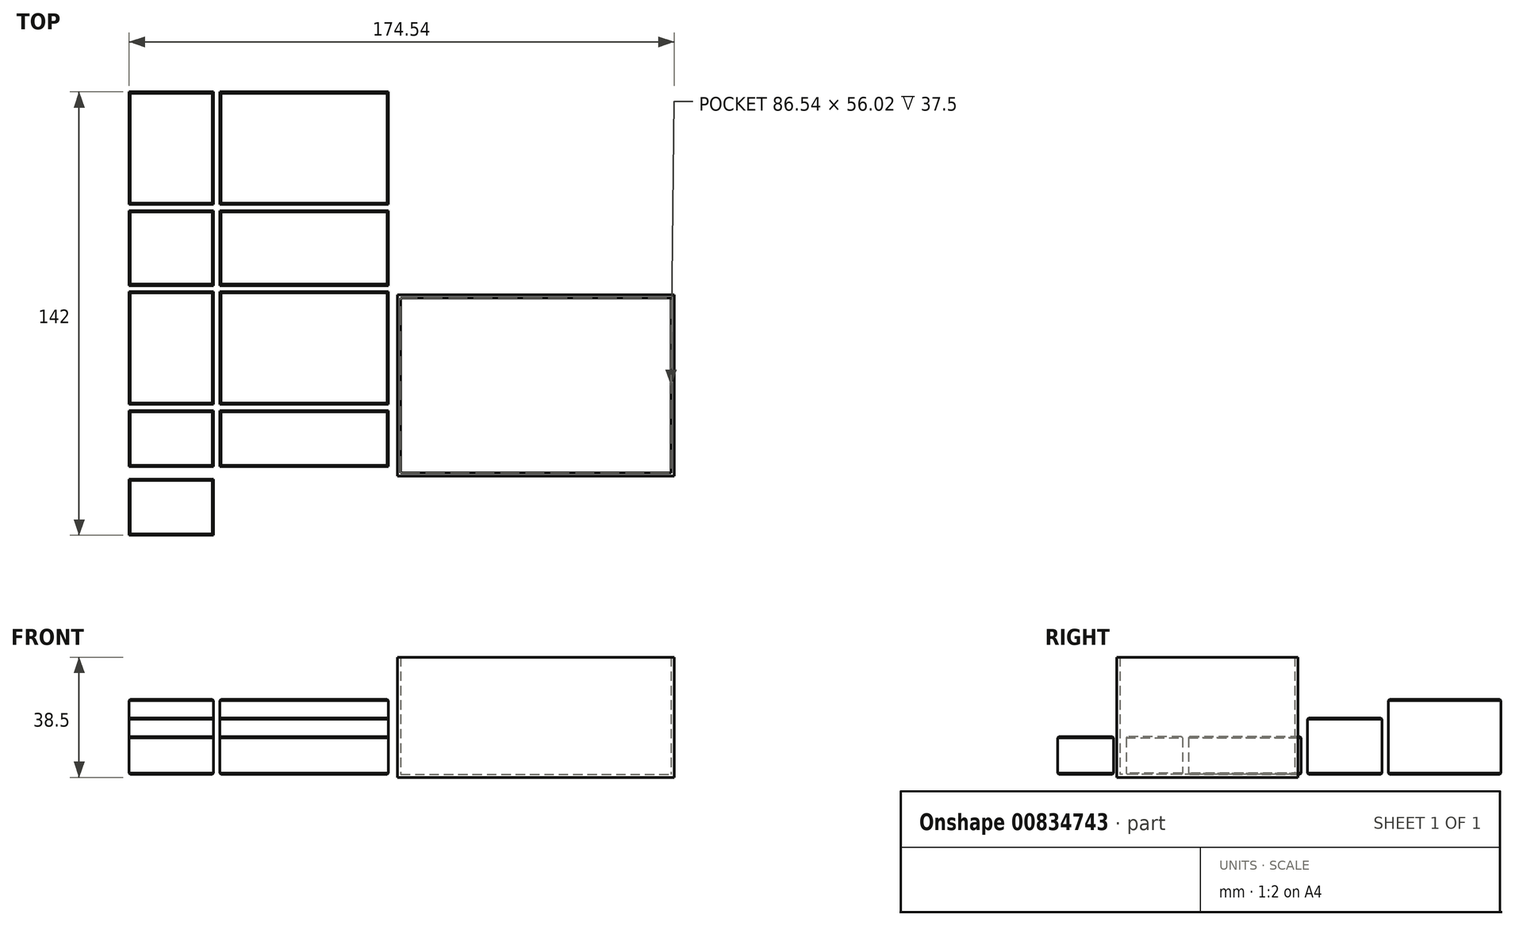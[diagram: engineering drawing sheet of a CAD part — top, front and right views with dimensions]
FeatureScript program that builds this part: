
annotation { "Feature Type Name" : "Feature", "Feature Type Description" : "" }
export const myFeature = defineFeature(function(context is Context, id is Id, definition is map)
    precondition{}
    {
        {
            assignVariable(context, id + "F0", {"name" : "L", "anyValue" : 84});
        }
        {
            assignVariable(context, id + "F1", {"name" : "W", "anyValue" : 9 * getVariable(context, 'L') / 14});
        }
        {
            assignVariable(context, id + "F2", {"name" : "H", "anyValue" : 3 * getVariable(context, 'L') / 7});
        }
        {
            assignVariable(context, id + "F3", {"name" : "A", "anyValue" : getVariable(context, 'L') / 7});
        }
        {
            assignVariable(context, id + "F4", {"name" : "B", "anyValue" : getVariable(context, 'W') / 2});
        }
        {
            assignVariable(context, id + "F5", {"name" : "C", "anyValue" : getVariable(context, 'H') / 2});
        }
        {
            assignVariable(context, id + "F6", {"name" : "NxtSDiff", "anyValue" : (5 * getVariable(context, 'A') + getVariable(context, 'B') - getVariable(context, 'L'))});
        }
        {
            assignVariable(context, id + "F7", {"name" : "H_Box", "anyValue" : getVariable(context, 'NxtSDiff') / 2 + getVariable(context, 'H')});
        }
        {
            assignVariable(context, id + "F8", {"name" : "T_Box", "anyValue" : 1});
        }
        {
            var Q0;
            Q0=qCreatedBy(makeId("Top.planeOp"),FACE);
            var sketch = newSketch(context, id + "F9", { "sketchPlane" : qUnion([Q0])});
            skLineSegment(sketch, "E0.bottom", {"start": v(-27, 20) * mm, "end": v(0, 20) * mm});
            skLineSegment(sketch, "E0.top", {"start": v(-27, 2) * mm, "end": v(0, 2) * mm});
            skLineSegment(sketch, "E0.left", {"start": v(-27, 20) * mm, "end": v(-27, 2) * mm});
            skLineSegment(sketch, "E0.right", {"start": v(0, 20) * mm, "end": v(0, 2) * mm});
            skLineSegment(sketch, "E1.bottom", {"start": v(2, 20) * mm, "end": v(56, 20) * mm});
            skLineSegment(sketch, "E1.top", {"start": v(2, 2) * mm, "end": v(56, 2) * mm});
            skLineSegment(sketch, "E1.left", {"start": v(2, 20) * mm, "end": v(2, 2) * mm});
            skLineSegment(sketch, "E1.right", {"start": v(56, 20) * mm, "end": v(56, 2) * mm});
            skLineSegment(sketch, "E2.bottom", {"start": v(-27, 58) * mm, "end": v(0, 58) * mm});
            skLineSegment(sketch, "E2.top", {"start": v(-27, 22) * mm, "end": v(0, 22) * mm});
            skLineSegment(sketch, "E2.left", {"start": v(-27, 58) * mm, "end": v(-27, 22) * mm});
            skLineSegment(sketch, "E2.right", {"start": v(0, 58) * mm, "end": v(0, 22) * mm});
            skLineSegment(sketch, "E3.bottom", {"start": v(2, 58) * mm, "end": v(56, 58) * mm});
            skLineSegment(sketch, "E3.top", {"start": v(2, 22) * mm, "end": v(56, 22) * mm});
            skLineSegment(sketch, "E3.left", {"start": v(2, 58) * mm, "end": v(2, 22) * mm});
            skLineSegment(sketch, "E3.right", {"start": v(56, 58) * mm, "end": v(56, 22) * mm});
            skLineSegment(sketch, "E4.bottom", {"start": v(-27, 84) * mm, "end": v(0, 84) * mm});
            skLineSegment(sketch, "E4.top", {"start": v(-27, 60) * mm, "end": v(0, 60) * mm});
            skLineSegment(sketch, "E4.left", {"start": v(-27, 84) * mm, "end": v(-27, 60) * mm});
            skLineSegment(sketch, "E4.right", {"start": v(0, 84) * mm, "end": v(0, 60) * mm});
            skLineSegment(sketch, "E5.bottom", {"start": v(2, 84) * mm, "end": v(56, 84) * mm});
            skLineSegment(sketch, "E5.top", {"start": v(2, 60) * mm, "end": v(56, 60) * mm});
            skLineSegment(sketch, "E5.left", {"start": v(2, 84) * mm, "end": v(2, 60) * mm});
            skLineSegment(sketch, "E5.right", {"start": v(56, 84) * mm, "end": v(56, 60) * mm});
            skLineSegment(sketch, "E6.bottom", {"start": v(-27, 122) * mm, "end": v(0, 122) * mm});
            skLineSegment(sketch, "E6.top", {"start": v(-27, 86) * mm, "end": v(0, 86) * mm});
            skLineSegment(sketch, "E6.left", {"start": v(-27, 122) * mm, "end": v(-27, 86) * mm});
            skLineSegment(sketch, "E6.right", {"start": v(0, 122) * mm, "end": v(0, 86) * mm});
            skLineSegment(sketch, "E7.bottom", {"start": v(2, 122) * mm, "end": v(56, 122) * mm});
            skLineSegment(sketch, "E7.top", {"start": v(2, 86) * mm, "end": v(56, 86) * mm});
            skLineSegment(sketch, "E7.left", {"start": v(2, 122) * mm, "end": v(2, 86) * mm});
            skLineSegment(sketch, "E7.right", {"start": v(56, 122) * mm, "end": v(56, 86) * mm});
            skLineSegment(sketch, "E8.MirrorCS", {"start": v(0, -20) * mm, "end": v(0, -2) * mm});
            skLineSegment(sketch, "E9.MirrorCS", {"start": v(-27, -2) * mm, "end": v(0, -2) * mm});
            skLineSegment(sketch, "E10.MirrorCS", {"start": v(-27, -20) * mm, "end": v(-27, -2) * mm});
            skLineSegment(sketch, "E11.MirrorCS", {"start": v(-27, -20) * mm, "end": v(0, -20) * mm});
            skLineSegment(sketch, "E12.bottom", {"start": v(60, 56.02) * mm, "end": v(146.54, 56.02) * mm});
            skLineSegment(sketch, "E12.top", {"start": v(60, 0) * mm, "end": v(146.54, 0) * mm});
            skLineSegment(sketch, "E12.left", {"start": v(60, 56.02) * mm, "end": v(60, 0) * mm});
            skLineSegment(sketch, "E12.right", {"start": v(146.54, 56.02) * mm, "end": v(146.54, 0) * mm});
            skSolve(sketch);
        }
        {
            var Q0;
            Q0=makeQuery(id+"F9.imprint","IMPRINT",FACE,{"disambiguationData":[TD([[makeQuery(id+"F9.imprint","IMPRINT",EDGE,{"derivedFrom":sQuery(id+"F9.wireOp",EDGE,"E0.bottom")}),-1.0]])]});
            var Q1;
            Q1=makeQuery(id+"F9.imprint","IMPRINT",FACE,{"disambiguationData":[TD([[makeQuery(id+"F9.imprint","IMPRINT",EDGE,{"derivedFrom":sQuery(id+"F9.wireOp",EDGE,"E2.bottom")}),-1.0]])]});
            var Q2;
            Q2=makeQuery(id+"F9.imprint","IMPRINT",FACE,{"disambiguationData":[TD([[makeQuery(id+"F9.imprint","IMPRINT",EDGE,{"derivedFrom":sQuery(id+"F9.wireOp",EDGE,"E3.bottom")}),-1.0]])]});
            var Q3;
            Q3=makeQuery(id+"F9.imprint","IMPRINT",FACE,{"disambiguationData":[TD([[makeQuery(id+"F9.imprint","IMPRINT",EDGE,{"derivedFrom":sQuery(id+"F9.wireOp",EDGE,"E1.bottom")}),-1.0]])]});
            extrude(context, id + "F10", {"entities" : qUnion([Q0, Q1, Q2, Q3]), "depth" : (getVariable(context, 'A')) * mm, "offsetDistance" : 25 * mm});
        }
        {
            var Q0;
            Q0=makeQuery(id+"F9.imprint","IMPRINT",FACE,{"disambiguationData":[TD([[makeQuery(id+"F9.imprint","IMPRINT",EDGE,{"derivedFrom":sQuery(id+"F9.wireOp",EDGE,"E4.bottom")}),-1.0]])]});
            var Q1;
            Q1=makeQuery(id+"F9.imprint","IMPRINT",FACE,{"disambiguationData":[TD([[makeQuery(id+"F9.imprint","IMPRINT",EDGE,{"derivedFrom":sQuery(id+"F9.wireOp",EDGE,"E5.bottom")}),-1.0]])]});
            extrude(context, id + "F11", {"entities" : qUnion([Q0, Q1]), "depth" : (getVariable(context, 'C')) * mm, "offsetDistance" : 25 * mm});
        }
        {
            var Q0;
            Q0=makeQuery(id+"F9.imprint","IMPRINT",FACE,{"disambiguationData":[TD([[makeQuery(id+"F9.imprint","IMPRINT",EDGE,{"derivedFrom":sQuery(id+"F9.wireOp",EDGE,"E6.bottom")}),-1.0]])]});
            var Q1;
            Q1=makeQuery(id+"F9.imprint","IMPRINT",FACE,{"disambiguationData":[TD([[makeQuery(id+"F9.imprint","IMPRINT",EDGE,{"derivedFrom":sQuery(id+"F9.wireOp",EDGE,"E7.bottom")}),-1.0]])]});
            extrude(context, id + "F12", {"entities" : qUnion([Q0, Q1]), "depth" : (2 * getVariable(context, 'A')) * mm, "offsetDistance" : 25 * mm});
        }
        {
            var Q0;
            Q0=makeQuery(id+"F9.imprint","IMPRINT",FACE,{"disambiguationData":[TD([[makeQuery(id+"F9.imprint","IMPRINT",EDGE,{"derivedFrom":sQuery(id+"F9.wireOp",EDGE,"E8.MirrorCS")}),1.0]])]});
            extrude(context, id + "F13", {"entities" : qUnion([Q0]), "depth" : (getVariable(context, 'A')) * mm, "offsetDistance" : 25 * mm});
        }
        {
            var Q0;
            Q0=makeQuery(id+"F12.opExtrude","CAP_FACE",FACE,{"disambiguationData":[OSD([sQuery(id+"F9.wireOp",EDGE,"E6.bottom"),sQuery(id+"F9.wireOp",EDGE,"E6.top"),sQuery(id+"F9.wireOp",EDGE,"E6.left"),sQuery(id+"F9.wireOp",EDGE,"E6.right")])],"isStart":false});
            var Q1;
            Q1=makeQuery(id+"F12.opExtrude","CAP_FACE",FACE,{"disambiguationData":[OSD([sQuery(id+"F9.wireOp",EDGE,"E7.bottom"),sQuery(id+"F9.wireOp",EDGE,"E7.top"),sQuery(id+"F9.wireOp",EDGE,"E7.left"),sQuery(id+"F9.wireOp",EDGE,"E7.right")])],"isStart":false});
            var Q2;
            Q2=makeQuery(id+"F11.opExtrude","CAP_FACE",FACE,{"disambiguationData":[OSD([sQuery(id+"F9.wireOp",EDGE,"E4.bottom"),sQuery(id+"F9.wireOp",EDGE,"E4.top"),sQuery(id+"F9.wireOp",EDGE,"E4.left"),sQuery(id+"F9.wireOp",EDGE,"E4.right")])],"isStart":false});
            var Q3;
            Q3=makeQuery(id+"F11.opExtrude","CAP_FACE",FACE,{"disambiguationData":[OSD([sQuery(id+"F9.wireOp",EDGE,"E5.bottom"),sQuery(id+"F9.wireOp",EDGE,"E5.top"),sQuery(id+"F9.wireOp",EDGE,"E5.left"),sQuery(id+"F9.wireOp",EDGE,"E5.right")])],"isStart":false});
            var Q4;
            Q4=makeQuery(id+"F10.opExtrude","CAP_FACE",FACE,{"disambiguationData":[OSD([sQuery(id+"F9.wireOp",EDGE,"E3.bottom"),sQuery(id+"F9.wireOp",EDGE,"E3.top"),sQuery(id+"F9.wireOp",EDGE,"E3.left"),sQuery(id+"F9.wireOp",EDGE,"E3.right")])],"isStart":false});
            var Q5;
            Q5=makeQuery(id+"F10.opExtrude","CAP_FACE",FACE,{"disambiguationData":[OSD([sQuery(id+"F9.wireOp",EDGE,"E2.bottom"),sQuery(id+"F9.wireOp",EDGE,"E2.top"),sQuery(id+"F9.wireOp",EDGE,"E2.left"),sQuery(id+"F9.wireOp",EDGE,"E2.right")])],"isStart":false});
            var Q6;
            Q6=makeQuery(id+"F10.opExtrude","CAP_FACE",FACE,{"disambiguationData":[OSD([sQuery(id+"F9.wireOp",EDGE,"E0.bottom"),sQuery(id+"F9.wireOp",EDGE,"E0.top"),sQuery(id+"F9.wireOp",EDGE,"E0.left"),sQuery(id+"F9.wireOp",EDGE,"E0.right")])],"isStart":false});
            var Q7;
            Q7=makeQuery(id+"F10.opExtrude","CAP_FACE",FACE,{"disambiguationData":[OSD([sQuery(id+"F9.wireOp",EDGE,"E1.bottom"),sQuery(id+"F9.wireOp",EDGE,"E1.top"),sQuery(id+"F9.wireOp",EDGE,"E1.left"),sQuery(id+"F9.wireOp",EDGE,"E1.right")])],"isStart":false});
            var Q8;
            Q8=makeQuery(id+"F13.opExtrude","CAP_FACE",FACE,{"disambiguationData":[OSD([sQuery(id+"F9.wireOp",EDGE,"E8.MirrorCS"),sQuery(id+"F9.wireOp",EDGE,"E9.MirrorCS"),sQuery(id+"F9.wireOp",EDGE,"E10.MirrorCS"),sQuery(id+"F9.wireOp",EDGE,"E11.MirrorCS")])],"isStart":false});
            var Q9;
            Q9=makeQuery(id+"F13.opExtrude","CAP_FACE",FACE,{"disambiguationData":[OSD([sQuery(id+"F9.wireOp",EDGE,"E8.MirrorCS"),sQuery(id+"F9.wireOp",EDGE,"E9.MirrorCS"),sQuery(id+"F9.wireOp",EDGE,"E10.MirrorCS"),sQuery(id+"F9.wireOp",EDGE,"E11.MirrorCS")])],"isStart":true});
            var Q10;
            Q10=makeQuery(id+"F10.opExtrude","CAP_FACE",FACE,{"disambiguationData":[OSD([sQuery(id+"F9.wireOp",EDGE,"E0.bottom"),sQuery(id+"F9.wireOp",EDGE,"E0.top"),sQuery(id+"F9.wireOp",EDGE,"E0.left"),sQuery(id+"F9.wireOp",EDGE,"E0.right")])],"isStart":true});
            var Q11;
            Q11=makeQuery(id+"F10.opExtrude","CAP_FACE",FACE,{"disambiguationData":[OSD([sQuery(id+"F9.wireOp",EDGE,"E1.bottom"),sQuery(id+"F9.wireOp",EDGE,"E1.top"),sQuery(id+"F9.wireOp",EDGE,"E1.left"),sQuery(id+"F9.wireOp",EDGE,"E1.right")])],"isStart":true});
            var Q12;
            Q12=makeQuery(id+"F10.opExtrude","CAP_FACE",FACE,{"disambiguationData":[OSD([sQuery(id+"F9.wireOp",EDGE,"E2.bottom"),sQuery(id+"F9.wireOp",EDGE,"E2.top"),sQuery(id+"F9.wireOp",EDGE,"E2.left"),sQuery(id+"F9.wireOp",EDGE,"E2.right")])],"isStart":true});
            var Q13;
            Q13=makeQuery(id+"F10.opExtrude","CAP_FACE",FACE,{"disambiguationData":[OSD([sQuery(id+"F9.wireOp",EDGE,"E3.bottom"),sQuery(id+"F9.wireOp",EDGE,"E3.top"),sQuery(id+"F9.wireOp",EDGE,"E3.left"),sQuery(id+"F9.wireOp",EDGE,"E3.right")])],"isStart":true});
            var Q14;
            Q14=makeQuery(id+"F11.opExtrude","CAP_FACE",FACE,{"disambiguationData":[OSD([sQuery(id+"F9.wireOp",EDGE,"E4.bottom"),sQuery(id+"F9.wireOp",EDGE,"E4.top"),sQuery(id+"F9.wireOp",EDGE,"E4.left"),sQuery(id+"F9.wireOp",EDGE,"E4.right")])],"isStart":true});
            var Q15;
            Q15=makeQuery(id+"F11.opExtrude","CAP_FACE",FACE,{"disambiguationData":[OSD([sQuery(id+"F9.wireOp",EDGE,"E5.bottom"),sQuery(id+"F9.wireOp",EDGE,"E5.top"),sQuery(id+"F9.wireOp",EDGE,"E5.left"),sQuery(id+"F9.wireOp",EDGE,"E5.right")])],"isStart":true});
            var Q16;
            Q16=makeQuery(id+"F12.opExtrude","CAP_FACE",FACE,{"disambiguationData":[OSD([sQuery(id+"F9.wireOp",EDGE,"E6.bottom"),sQuery(id+"F9.wireOp",EDGE,"E6.top"),sQuery(id+"F9.wireOp",EDGE,"E6.left"),sQuery(id+"F9.wireOp",EDGE,"E6.right")])],"isStart":true});
            var Q17;
            Q17=makeQuery(id+"F12.opExtrude","CAP_FACE",FACE,{"disambiguationData":[OSD([sQuery(id+"F9.wireOp",EDGE,"E7.bottom"),sQuery(id+"F9.wireOp",EDGE,"E7.top"),sQuery(id+"F9.wireOp",EDGE,"E7.left"),sQuery(id+"F9.wireOp",EDGE,"E7.right")])],"isStart":true});
            chamfer(context, id + "F14", {"entities" : qUnion([Q0, Q1, Q2, Q3, Q4, Q5, Q6, Q7, Q8, Q9, Q10, Q11, Q12, Q13, Q14, Q15, Q16, Q17]), "width" : 0.4 * mm, "tangentPropagation" : true});
        }
        {
            var Q0;
            Q0=makeQuery(id+"F9.imprint","IMPRINT",FACE,{"disambiguationData":[TD([[makeQuery(id+"F9.imprint","IMPRINT",EDGE,{"derivedFrom":sQuery(id+"F9.wireOp",EDGE,"E12.bottom")}),-1.0]])]});
            extrude(context, id + "F15", {"entities" : qUnion([Q0]), "depth" : (getVariable(context, 'H_Box')) * mm, "offsetDistance" : 25 * mm});
        }
        {
            var Q0;
            Q0=makeQuery(id+"F15.opExtrude","CAP_FACE",FACE,{"disambiguationData":[OSD([sQuery(id+"F9.wireOp",EDGE,"E12.bottom"),sQuery(id+"F9.wireOp",EDGE,"E12.top"),sQuery(id+"F9.wireOp",EDGE,"E12.left"),sQuery(id+"F9.wireOp",EDGE,"E12.right")])],"isStart":false});
            shell(context, id + "F16", {"entities" : qUnion([Q0]), "thickness" : (getVariable(context, 'T_Box')) * mm, "oppositeDirection" : true});
        }
    });
